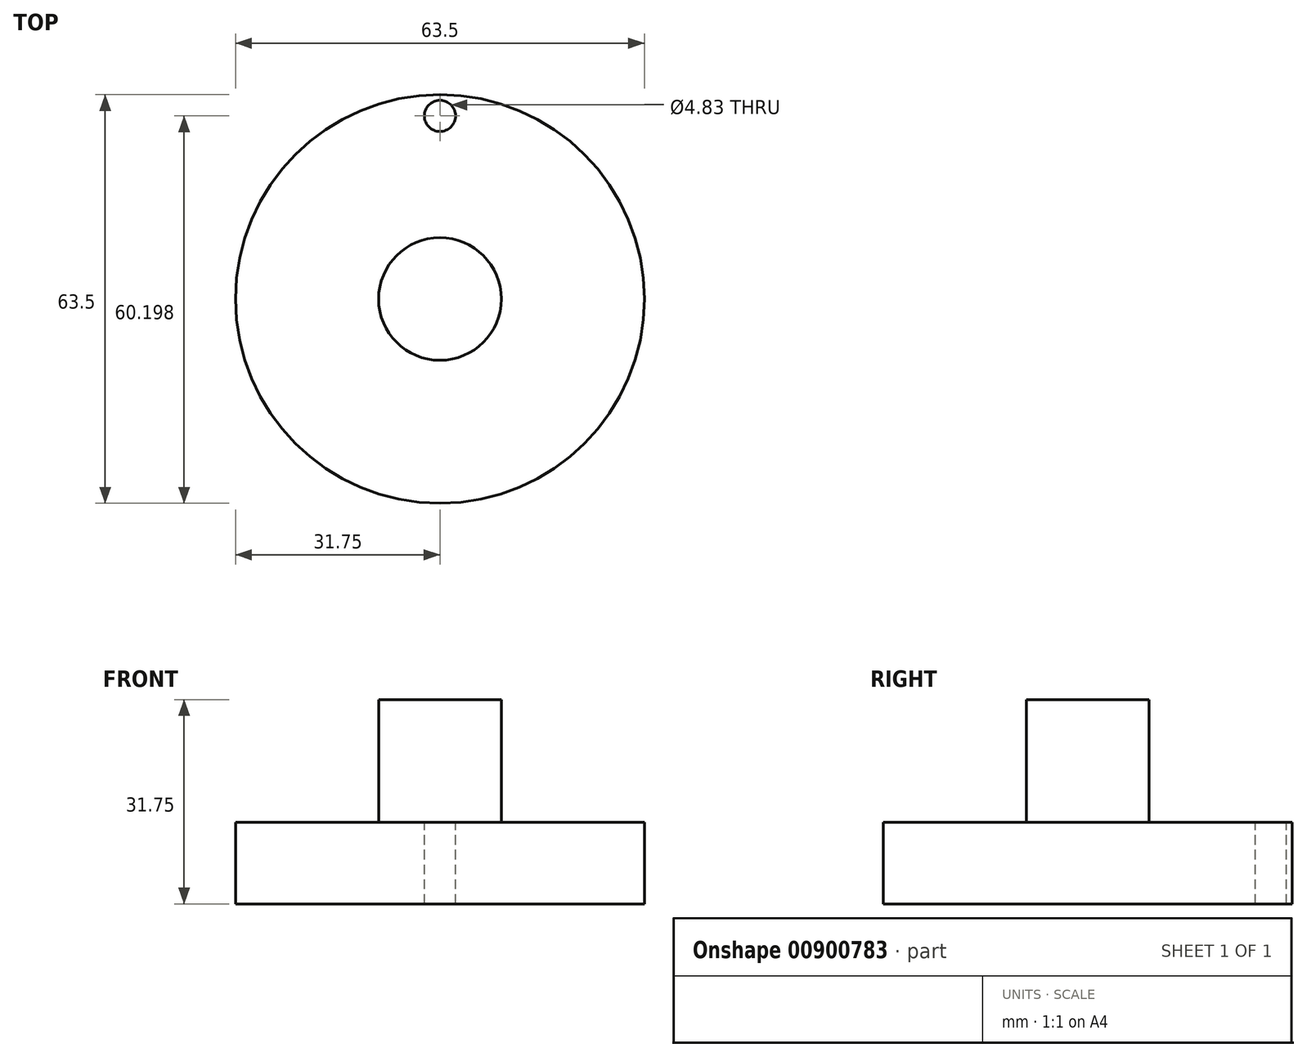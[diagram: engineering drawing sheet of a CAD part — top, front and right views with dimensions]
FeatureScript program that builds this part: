
annotation { "Feature Type Name" : "Feature", "Feature Type Description" : "" }
export const myFeature = defineFeature(function(context is Context, id is Id, definition is map)
    precondition{}
    {
        {
            var Q0;
            Q0=qCreatedBy(makeId("Front.planeOp"),FACE);
            var sketch = newSketch(context, id + "F0", { "sketchPlane" : qUnion([Q0])});
            skLineSegment(sketch, "E0", {"start": v(0, 0) * mm, "end": v(-31.75, 0) * mm});
            skLineSegment(sketch, "E1", {"start": v(-31.75, 0) * mm, "end": v(-31.75, 12.7) * mm});
            skLineSegment(sketch, "E2", {"start": v(-31.75, 12.7) * mm, "end": v(-9.52, 12.7) * mm});
            skLineSegment(sketch, "E3", {"start": v(-9.53, 12.7) * mm, "end": v(-9.53, 31.75) * mm});
            skLineSegment(sketch, "E4", {"start": v(-9.53, 31.75) * mm, "end": v(0, 31.75) * mm});
            skLineSegment(sketch, "E5", {"start": v(0, 31.75) * mm, "end": v(0, 0) * mm});
            skSolve(sketch);
        }
        {
            var Q0;
            Q0=makeQuery(id+"F0.imprint","IMPRINT",FACE,{"disambiguationData":[TD([[makeQuery(id+"F0.imprint","IMPRINT",EDGE,{"derivedFrom":sQuery(id+"F0.wireOp",EDGE,"E0")}),-1.0]])]});
            var Q1;
            Q1=sQuery(id+"F0.wireOp",EDGE,"E5");
            revolve(context, id + "F1", {"surfaceOperationType" : NewSurfaceOperationType.NEW, "entities" : qUnion([Q0]), "axis" : qUnion([Q1]), "revolveType" : RevolveType.FULL});
        }
        {
            var Q0;
            Q0=makeQuery(id+"F1.opRevolve","SWEPT_FACE",FACE,{"disambiguationData":[OSD([sQuery(id+"F0.wireOp",EDGE,"E2")])]});
            var sketch = newSketch(context, id + "F2", { "sketchPlane" : qUnion([Q0])});
            skPoint(sketch, "E6", {"position": v(0, 28.45) * mm});
            skSolve(sketch);
        }
        {
            var Q0;
            Q0=sQuery(id+"F2.wireOp",VERTEX,"E6");
            var Q1;
            Q1=makeQuery(id+"F1.opRevolve","SWEPT_BODY",BODY,{"disambiguationData":[OSD([sQuery(id+"F0.wireOp",EDGE,"E0"),sQuery(id+"F0.wireOp",EDGE,"E1"),sQuery(id+"F0.wireOp",EDGE,"E2"),sQuery(id+"F0.wireOp",EDGE,"E3"),sQuery(id+"F0.wireOp",EDGE,"E4"),sQuery(id+"F0.wireOp",EDGE,"E5")])]});
            hole(context, id + "F3", {"style" : HoleStyle.SIMPLE, "endStyle" : HoleEndStyle.THROUGH, "holeDiameter" : 4.83 * mm, "majorDiameter" : 6.35 * mm, "isTappedThrough" : true, "tappedDepth" : 12.7 * mm, "tapClearance" : 3, "locations" : qUnion([Q0]), "scope" : qUnion([Q1])});
        }
    });
